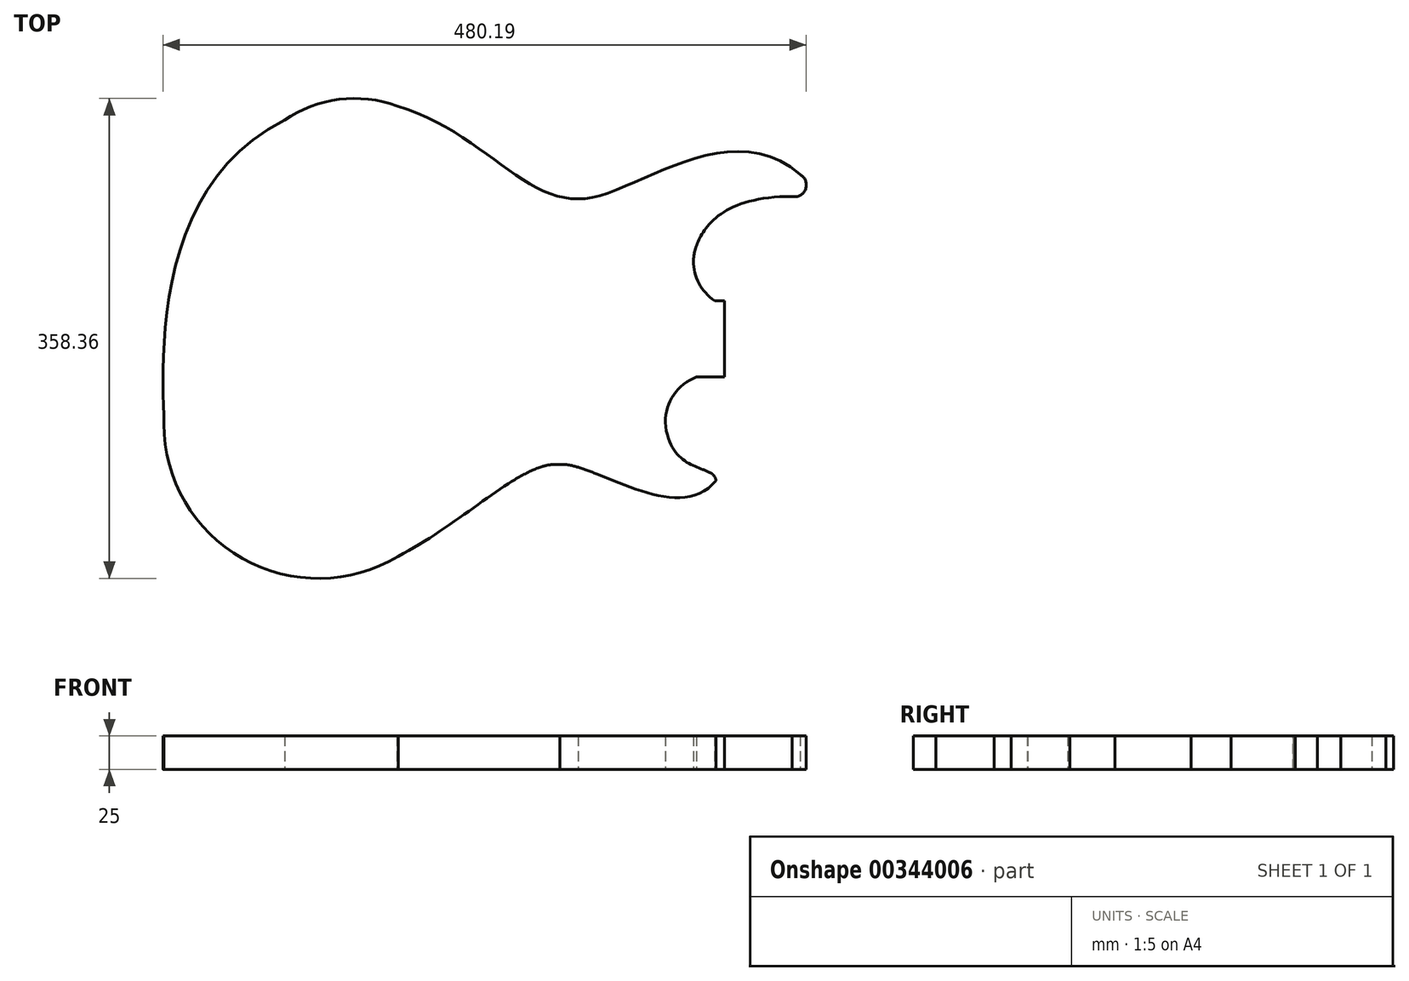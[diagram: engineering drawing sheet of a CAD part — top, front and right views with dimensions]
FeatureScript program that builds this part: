
annotation { "Feature Type Name" : "Feature", "Feature Type Description" : "" }
export const myFeature = defineFeature(function(context is Context, id is Id, definition is map)
    precondition{}
    {
        {
            var Q0;
            Q0=qCreatedBy(makeId("Top.planeOp"),FACE);
            var sketch = newSketch(context, id + "F0", { "sketchPlane" : qUnion([Q0])});
            skCircle(sketch, "E0", {"center": v(192.48, -62.28) * mm, "radius": 36.2 * mm});
            skCircle(sketch, "E1", {"center": v(-102.6, -63.61) * mm, "radius": 115.26 * mm});
            skCircle(sketch, "E2", {"center": v(-75.51, 87.15) * mm, "radius": 92.33 * mm});
            skCircle(sketch, "E3", {"center": v(91.31, 159.03) * mm, "radius": 54.4 * mm});
            skCircle(sketch, "E4", {"center": v(213.4, 58.33) * mm, "radius": 36.08 * mm});
            skCircle(sketch, "E5", {"center": v(77.57, -152.67) * mm, "radius": 58.79 * mm});
            skFitSpline(sketch, "E6", {"points": [v(-102.6, -178.88) * mm, v(77.57, -93.88) * mm], "startDerivative": vector(223.46, 0) * mm, "endDerivative": vector(112.96, -14.48) * mm});
            skFitSpline(sketch, "E7", {"points": [v(77.57, -93.88) * mm, v(194.12, -105.79) * mm], "startDerivative": vector(71.1, 8.76) * mm, "endDerivative": vector(87.1, 106.87) * mm});
            skFitSpline(sketch, "E8", {"points": [v(194.12, -105.79) * mm, v(156.28, -62.28) * mm], "startDerivative": vector(-2.7, 38.17) * mm, "endDerivative": vector(-11.35, 119.65) * mm});
            skLineSegment(sketch, "E9.bottom", {"start": v(200.69, 28.5) * mm, "end": v(132.35, 28.5) * mm});
            skLineSegment(sketch, "E9.top", {"start": v(200.69, -28.5) * mm, "end": v(132.35, -28.5) * mm});
            skLineSegment(sketch, "E9.left", {"start": v(200.69, 28.5) * mm, "end": v(200.69, -28.5) * mm});
            skLineSegment(sketch, "E9.right", {"start": v(132.35, 28.5) * mm, "end": v(132.35, -28.5) * mm});
            skFitSpline(sketch, "E10", {"points": [v(-217.86, -63.61) * mm, v(-75.51, 179.48) * mm], "startDerivative": vector(-4.48, 159.79) * mm, "endDerivative": vector(463.55, 74.43) * mm});
            skFitSpline(sketch, "E11", {"points": [v(-75.51, 179.48) * mm, v(91.31, 104.62) * mm], "startDerivative": vector(246.55, -15.73) * mm, "endDerivative": vector(142.2, 5.1) * mm});
            skFitSpline(sketch, "E12", {"points": [v(257.08, 122.64) * mm, v(91.31, 104.62) * mm], "startDerivative": vector(-168.67, 145.2) * mm, "endDerivative": vector(-111.42, 6.92) * mm});
            skFitSpline(sketch, "E13", {"points": [v(251, 106.23) * mm, v(177.33, 58.33) * mm], "startDerivative": vector(-211.1, 2.1) * mm, "endDerivative": vector(-0.35, -11.64) * mm});
            skCircle(sketch, "E14", {"center": v(252.76, 114.91) * mm, "radius": 8.86 * mm});
            skPoint(sketch, "E14.second.point", {"position": v(261.6, 114.27) * mm});
            skSolve(sketch);
        }
        {
            var Q0;
            {var subQ0=sQuery(id+"F0.wireOp",EDGE,"E6");var subQ1=sQuery(id+"F0.wireOp",EDGE,"E1");var subQ2=makeQuery(id+"F0.imprint","INTERSECT",VERTEX,{"disambiguationData":[OD(0.0)],"derivedFrom":[subQ1,subQ0]});Q0=makeQuery(id+"F0.imprint","IMPRINT",FACE,{"disambiguationData":[TD([[makeQuery(id+"F0.imprint","IMPRINT",EDGE,{"disambiguationData":[TD([[subQ2,-1.0]])],"derivedFrom":subQ1}),1.0]])]});}
            var Q1;
            {var subQ0=sQuery(id+"F0.wireOp",EDGE,"E11");var subQ1=sQuery(id+"F0.wireOp",EDGE,"E2");var subQ3=makeQuery(id+"F0.imprint","INTERSECT",VERTEX,{"derivedFrom":[subQ1,subQ0]});Q1=makeQuery(id+"F0.imprint","IMPRINT",FACE,{"disambiguationData":[TD([[makeQuery(id+"F0.imprint","IMPRINT",EDGE,{"disambiguationData":[TD([[subQ3,-1.0]])],"derivedFrom":subQ1}),1.0]])]});}
            var Q2;
            {var subQ0=sQuery(id+"F0.wireOp",EDGE,"E10");var subQ1=sQuery(id+"F0.wireOp",EDGE,"E2");var subQ3=makeQuery(id+"F0.imprint","INTERSECT",VERTEX,{"derivedFrom":[subQ1,subQ0]});Q2=makeQuery(id+"F0.imprint","IMPRINT",FACE,{"disambiguationData":[TD([[makeQuery(id+"F0.imprint","IMPRINT",EDGE,{"disambiguationData":[TD([[subQ3,1.0]])],"derivedFrom":subQ1}),1.0]])]});}
            var Q3;
            {var subQ0=sQuery(id+"F0.wireOp",EDGE,"E14");var subQ1=makeQuery(id+"F0.imprint","INTERSECT",VERTEX,{"derivedFrom":[sQuery(id+"F0.wireOp",EDGE,"E12"),subQ0]});Q3=makeQuery(id+"F0.imprint","IMPRINT",FACE,{"disambiguationData":[TD([[makeQuery(id+"F0.imprint","IMPRINT",EDGE,{"disambiguationData":[TD([[subQ1,-1.0]])],"derivedFrom":subQ0}),1.0]])]});}
            var Q4;
            {var subQ0=sQuery(id+"F0.wireOp",EDGE,"E9.left");var subQ1=sQuery(id+"F0.wireOp",EDGE,"E0");var subQ2=makeQuery(id+"F0.imprint","INTERSECT",VERTEX,{"derivedFrom":[subQ1,subQ0]});Q4=makeQuery(id+"F0.imprint","IMPRINT",FACE,{"disambiguationData":[TD([[makeQuery(id+"F0.imprint","IMPRINT",EDGE,{"disambiguationData":[TD([[subQ2,-1.0]])],"derivedFrom":subQ1}),1.0]])]});}
            var Q5;
            {var subQ0=sQuery(id+"F0.wireOp",EDGE,"E8");var subQ1=sQuery(id+"F0.wireOp",EDGE,"E0");var subQ2=makeQuery(id+"F0.imprint","INTERSECT",VERTEX,{"disambiguationData":[OD(0.0)],"derivedFrom":[subQ1,subQ0]});Q5=makeQuery(id+"F0.imprint","IMPRINT",FACE,{"disambiguationData":[TD([[makeQuery(id+"F0.imprint","IMPRINT",EDGE,{"disambiguationData":[TD([[subQ2,-1.0]])],"derivedFrom":subQ1}),1.0]])]});}
            var Q6;
            {var subQ0=sQuery(id+"F0.wireOp",EDGE,"E13");var subQ1=sQuery(id+"F0.wireOp",EDGE,"E4");var subQ2=makeQuery(id+"F0.imprint","INTERSECT",VERTEX,{"disambiguationData":[OD(0.0)],"derivedFrom":[subQ1,subQ0]});Q6=makeQuery(id+"F0.imprint","IMPRINT",FACE,{"disambiguationData":[TD([[makeQuery(id+"F0.imprint","IMPRINT",EDGE,{"disambiguationData":[TD([[subQ2,1.0]])],"derivedFrom":subQ1}),1.0]])]});}
            var Q7;
            {var subQ0=sQuery(id+"F0.wireOp",EDGE,"E9.left");var subQ1=sQuery(id+"F0.wireOp",EDGE,"E4");var subQ2=makeQuery(id+"F0.imprint","INTERSECT",VERTEX,{"derivedFrom":[subQ1,subQ0]});Q7=makeQuery(id+"F0.imprint","IMPRINT",FACE,{"disambiguationData":[TD([[makeQuery(id+"F0.imprint","IMPRINT",EDGE,{"disambiguationData":[TD([[subQ2,1.0]])],"derivedFrom":subQ1}),1.0]])]});}
            var Q8;
            {var subQ0=sQuery(id+"F0.wireOp",EDGE,"E7");var subQ1=sQuery(id+"F0.wireOp",EDGE,"E5");var subQ2=makeQuery(id+"F0.imprint","INTERSECT",VERTEX,{"disambiguationData":[OD(0.0)],"derivedFrom":[subQ1,subQ0]});Q8=makeQuery(id+"F0.imprint","IMPRINT",FACE,{"disambiguationData":[TD([[makeQuery(id+"F0.imprint","IMPRINT",EDGE,{"disambiguationData":[TD([[subQ2,-1.0]])],"derivedFrom":subQ1}),1.0]])]});}
            var Q9;
            {var subQ0=sQuery(id+"F0.wireOp",EDGE,"E6");var subQ1=sQuery(id+"F0.wireOp",EDGE,"E5");var subQ2=makeQuery(id+"F0.imprint","INTERSECT",VERTEX,{"disambiguationData":[OD(0.0)],"derivedFrom":[subQ1,subQ0]});Q9=makeQuery(id+"F0.imprint","IMPRINT",FACE,{"disambiguationData":[TD([[makeQuery(id+"F0.imprint","IMPRINT",EDGE,{"disambiguationData":[TD([[subQ2,1.0]])],"derivedFrom":subQ1}),1.0]])]});}
            var Q10;
            {var subQ0=sQuery(id+"F0.wireOp",EDGE,"E9.right");Q10=makeQuery(id+"F0.imprint","IMPRINT",FACE,{"disambiguationData":[TD([[makeQuery(id+"F0.imprint","IMPRINT",EDGE,{"derivedFrom":subQ0}),1.0]])]});}
            var Q11;
            {var subQ1=sQuery(id+"F0.wireOp",EDGE,"E1");var subQ7=makeQuery(id+"F0.imprint","INTERSECT",VERTEX,{"derivedFrom":[subQ1,sQuery(id+"F0.wireOp",EDGE,"E10")]});Q11=makeQuery(id+"F0.imprint","IMPRINT",FACE,{"disambiguationData":[TD([[makeQuery(id+"F0.imprint","IMPRINT",EDGE,{"disambiguationData":[TD([[subQ7,1.0]])],"derivedFrom":subQ1}),1.0]])]});}
            var Q12;
            {var subQ30=sQuery(id+"F0.wireOp",EDGE,"E9.right");Q12=makeQuery(id+"F0.imprint","IMPRINT",FACE,{"disambiguationData":[TD([[makeQuery(id+"F0.imprint","IMPRINT",EDGE,{"derivedFrom":subQ30}),-1.0]])]});}
            var Q13;
            {var subQ0=sQuery(id+"F0.wireOp",EDGE,"E10");var subQ1=sQuery(id+"F0.wireOp",EDGE,"E1");var subQ2=makeQuery(id+"F0.imprint","INTERSECT",VERTEX,{"derivedFrom":[subQ1,subQ0]});Q13=makeQuery(id+"F0.imprint","IMPRINT",FACE,{"disambiguationData":[TD([[makeQuery(id+"F0.imprint","IMPRINT",EDGE,{"disambiguationData":[TD([[subQ2,1.0]])],"derivedFrom":subQ1}),-1.0]])]});}
            var Q14;
            {var subQ2=sQuery(id+"F0.wireOp",EDGE,"E2");var subQ6=sQuery(id+"F0.wireOp",EDGE,"E1");var subQ8=makeQuery(id+"F0.imprint","INTERSECT",VERTEX,{"disambiguationData":[OD(0.0)],"derivedFrom":[subQ6,subQ2]});Q14=makeQuery(id+"F0.imprint","IMPRINT",FACE,{"disambiguationData":[TD([[makeQuery(id+"F0.imprint","IMPRINT",EDGE,{"disambiguationData":[TD([[subQ8,1.0]])],"derivedFrom":subQ6}),-1.0]])]});}
            var Q15;
            {var subQ0=sQuery(id+"F0.wireOp",EDGE,"E2");var subQ1=sQuery(id+"F0.wireOp",EDGE,"E1");var subQ2=makeQuery(id+"F0.imprint","INTERSECT",VERTEX,{"disambiguationData":[OD(0.0)],"derivedFrom":[subQ1,subQ0]});Q15=makeQuery(id+"F0.imprint","IMPRINT",FACE,{"disambiguationData":[TD([[makeQuery(id+"F0.imprint","IMPRINT",EDGE,{"disambiguationData":[TD([[subQ2,1.0]])],"derivedFrom":subQ1}),1.0]])]});}
            extrude(context, id + "F1", {"entities" : qUnion([Q0, Q1, Q2, Q3, Q4, Q5, Q6, Q7, Q8, Q9, Q10, Q11, Q12, Q13, Q14, Q15]), "depth" : 25 * mm});
        }
    });
